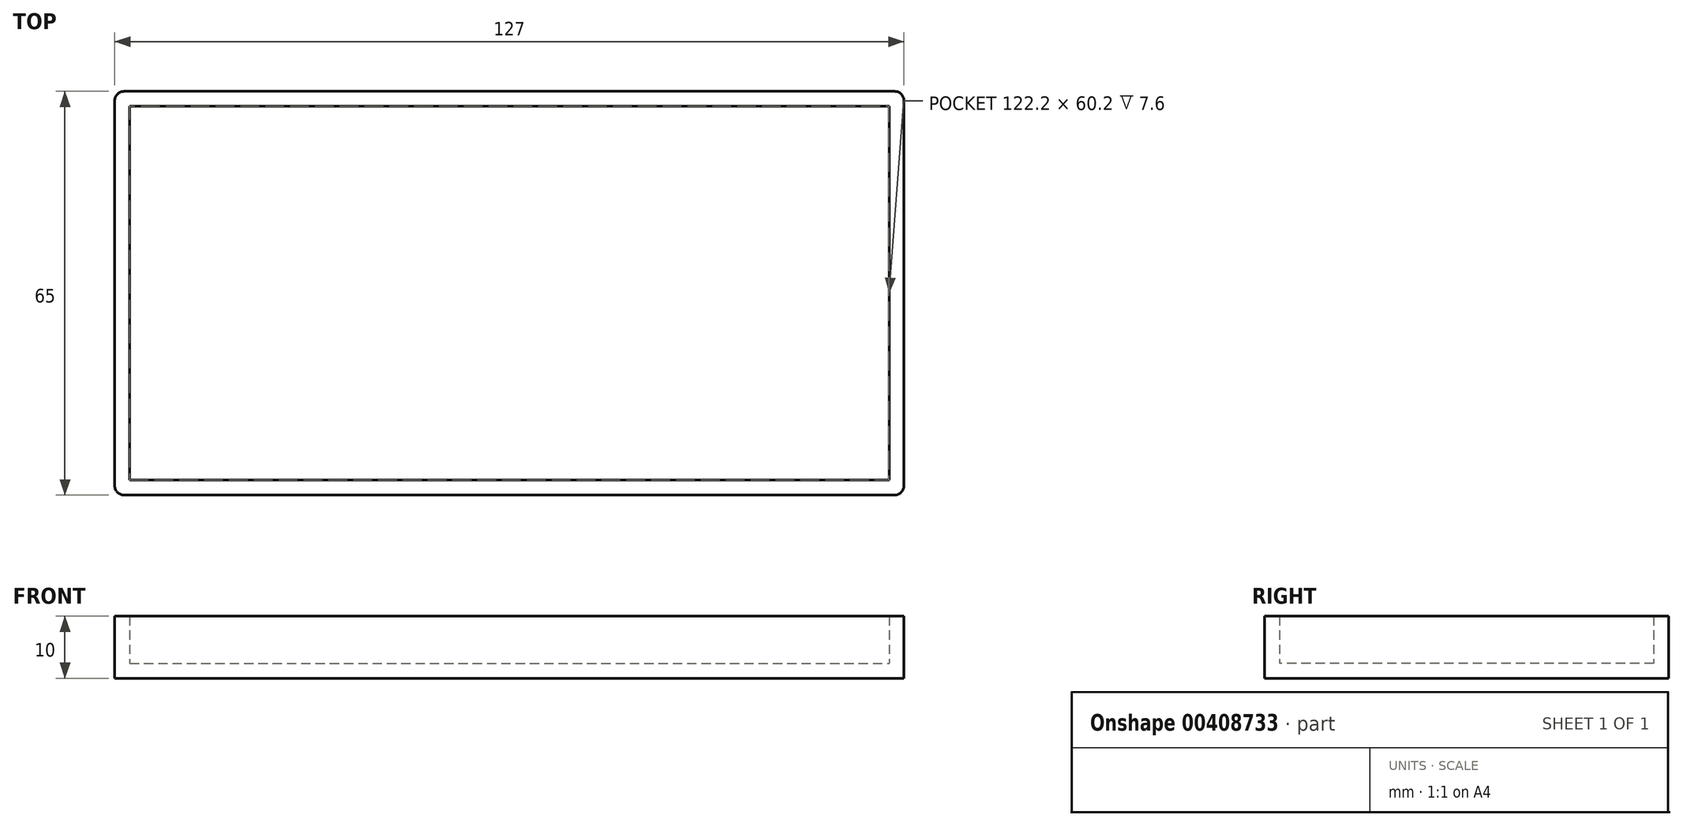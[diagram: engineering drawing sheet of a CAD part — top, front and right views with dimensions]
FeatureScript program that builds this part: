
annotation { "Feature Type Name" : "Feature", "Feature Type Description" : "" }
export const myFeature = defineFeature(function(context is Context, id is Id, definition is map)
    precondition{}
    {
        {
            assignVariable(context, id + "F0", {"name" : "defaultThickness", "anyValue" : 2.4 * mm});
        }
        {
            var Q0;
            Q0=qCreatedBy(makeId("Top.planeOp"),FACE);
            var sketch = newSketch(context, id + "F1", { "sketchPlane" : qUnion([Q0])});
            skLineSegment(sketch, "E0.bottom", {"start": v(-63.5, 32.5) * mm, "end": v(63.5, 32.5) * mm});
            skLineSegment(sketch, "E0.top", {"start": v(-63.5, -32.5) * mm, "end": v(63.5, -32.5) * mm});
            skLineSegment(sketch, "E0.left", {"start": v(-63.5, 32.5) * mm, "end": v(-63.5, -32.5) * mm});
            skLineSegment(sketch, "E0.right", {"start": v(63.5, 32.5) * mm, "end": v(63.5, -32.5) * mm});
            skPoint(sketch, "E0.middle", {"position": v(0, 0) * mm});
            skLineSegment(sketch, "E1.0", {"start": v(-61.1, 30.1) * mm, "end": v(61.1, 30.1) * mm});
            skLineSegment(sketch, "E1.1", {"start": v(-61.1, 30.1) * mm, "end": v(-61.1, -30.1) * mm});
            skLineSegment(sketch, "E1.2", {"start": v(-61.1, -30.1) * mm, "end": v(61.1, -30.1) * mm});
            skLineSegment(sketch, "E1.3", {"start": v(61.1, 30.1) * mm, "end": v(61.1, -30.1) * mm});
            skSolve(sketch);
        }
        {
            var Q0;
            Q0 = qSketchRegion(id + "F1", true);
            extrude(context, id + "F2", {"entities" : qUnion([Q0]), "depth" : 10 * mm});
        }
        {
            var Q0;
            Q0=makeQuery(id+"F1.imprint","IMPRINT",FACE,{"disambiguationData":[TD([[makeQuery(id+"F1.imprint","IMPRINT",EDGE,{"derivedFrom":sQuery(id+"F1.wireOp",EDGE,"E1.0")}),-1.0]])]});
            extrude(context, id + "F3", {"entities" : qUnion([Q0]), "operationType" : NewBodyOperationType.ADD, "depth" : getVariable(context, 'defaultThickness')});
        }
        {
            var Q0;
            Q0=makeQuery(id+"F2.opExtrude","SWEPT_EDGE",EDGE,{"disambiguationData":[OSD([sQuery(id+"F1.wireOp",EDGE,"E0.top"),sQuery(id+"F1.wireOp",EDGE,"E0.right")])]});
            var Q1;
            Q1=makeQuery(id+"F2.opExtrude","SWEPT_EDGE",EDGE,{"disambiguationData":[OSD([sQuery(id+"F1.wireOp",EDGE,"E0.bottom"),sQuery(id+"F1.wireOp",EDGE,"E0.right")])]});
            var Q2;
            Q2=makeQuery(id+"F2.opExtrude","SWEPT_EDGE",EDGE,{"disambiguationData":[OSD([sQuery(id+"F1.wireOp",EDGE,"E0.bottom"),sQuery(id+"F1.wireOp",EDGE,"E0.left")])]});
            var Q3;
            Q3=makeQuery(id+"F2.opExtrude","SWEPT_EDGE",EDGE,{"disambiguationData":[OSD([sQuery(id+"F1.wireOp",EDGE,"E0.top"),sQuery(id+"F1.wireOp",EDGE,"E0.left")])]});
            fillet(context, id + "F4", {"entities" : qUnion([Q0, Q1, Q2, Q3]), "radius" : 1.5 * mm, "tangentPropagation" : true, "allowEdgeOverflow" : false});
        }
    });
